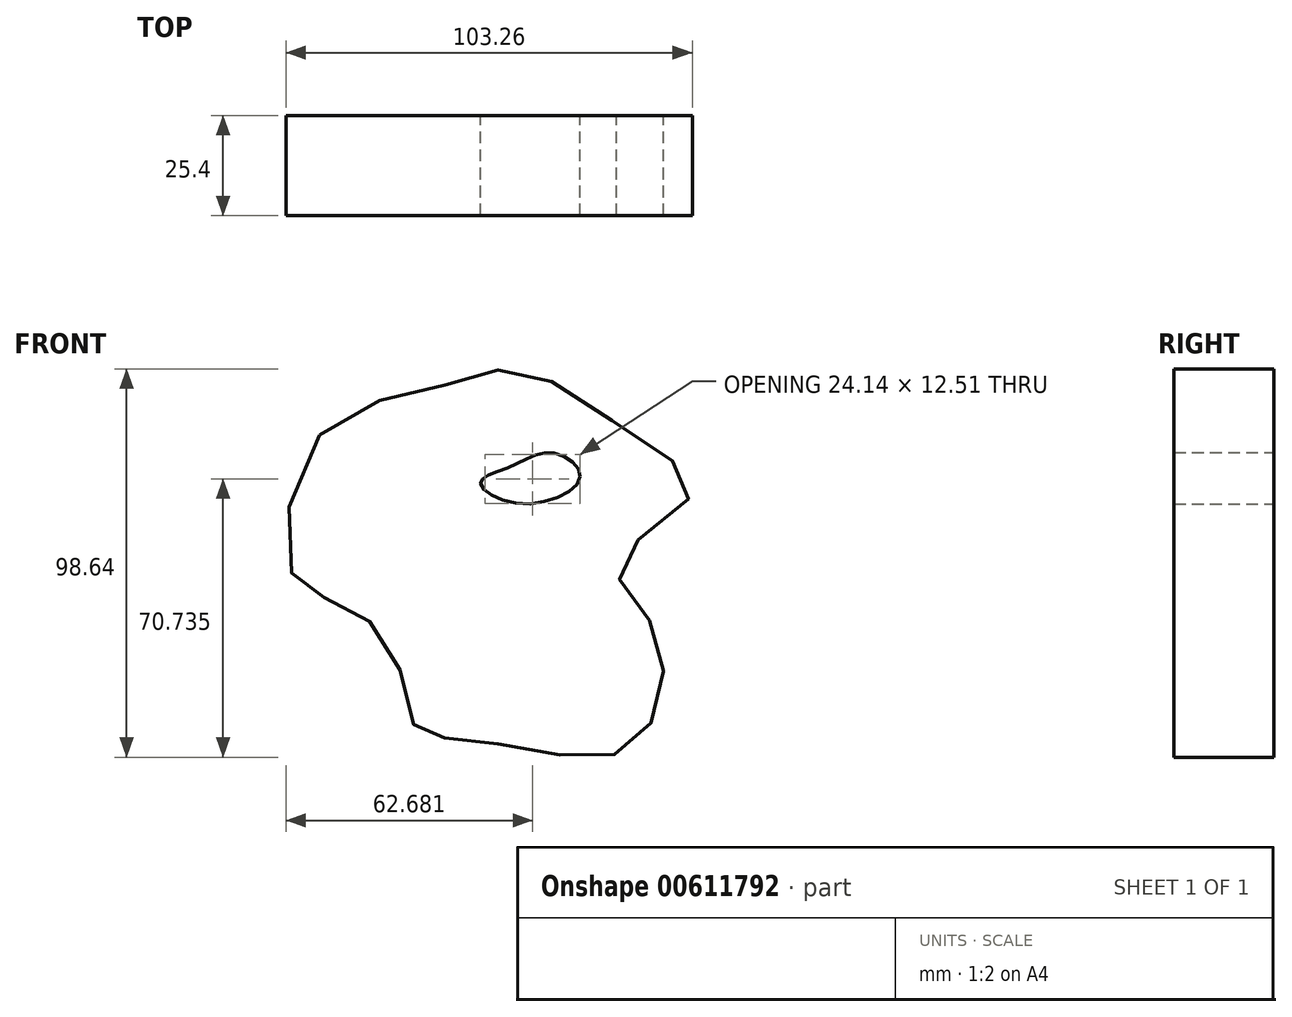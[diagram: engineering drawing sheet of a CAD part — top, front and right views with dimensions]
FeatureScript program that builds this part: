
annotation { "Feature Type Name" : "Feature", "Feature Type Description" : "" }
export const myFeature = defineFeature(function(context is Context, id is Id, definition is map)
    precondition{}
    {
        {
            var Q0;
            Q0=qCreatedBy(makeId("Front.planeOp"),FACE);
            var sketch = newSketch(context, id + "F0", { "sketchPlane" : qUnion([Q0])});
            skFitSpline(sketch, "E0", {"points": [v(-59.1, 47.37) * mm, v(-66.32, 12.48) * mm, v(-56.4, 5.56) * mm, v(-40.76, -6.77) * mm, v(-34.44, -27.52) * mm, v(-25.12, -29.63) * mm, v(0, -33.54) * mm, v(19.7, -32.03) * mm, v(28.12, -15.5) * mm, v(23.01, 2.86) * mm, v(16.7, 15.19) * mm, v(35.34, 32.64) * mm, v(20.6, 47.37) * mm, v(-8.27, 63.92) * mm, v(-28.73, 59.7) * mm, v(-59.1, 47.37) * mm]});
            skSolve(sketch);
        }
        {
            var Q0;
            Q0=makeQuery(id+"F0.imprint","IMPRINT",FACE,{"disambiguationData":[TD([[makeQuery(id+"F0.imprint","IMPRINT",EDGE,{"derivedFrom":sQuery(id+"F0.wireOp",EDGE,"E0")}),1.0]])]});
            extrude(context, id + "F1", {"entities" : qUnion([Q0]), "depth" : 25.4 * mm, "offsetDistance" : 25.4 * mm});
        }
        {
            var Q0;
            Q0=makeQuery(id+"F1.opExtrude","CAP_FACE",FACE,{"disambiguationData":[OSD([sQuery(id+"F0.wireOp",EDGE,"E0")])],"isStart":true});
            var sketch = newSketch(context, id + "F2", { "sketchPlane" : qUnion([Q0])});
            skFitSpline(sketch, "E1", {"points": [v(-7.07, 36.85) * mm, v(0, 42.86) * mm, v(10.98, 39.25) * mm, v(18.2, 35.34) * mm, v(7.67, 29.93) * mm, v(-7.07, 36.85) * mm]});
            skSolve(sketch);
        }
        {
            var Q0;
            Q0=makeQuery(id+"F2.imprint","IMPRINT",FACE,{"disambiguationData":[TD([[makeQuery(id+"F2.imprint","IMPRINT",EDGE,{"derivedFrom":sQuery(id+"F2.wireOp",EDGE,"E1")}),-1.0]])]});
            extrude(context, id + "F3", {"entities" : qUnion([Q0]), "operationType" : NewBodyOperationType.REMOVE, "oppositeDirection" : true, "depth" : 25.4 * mm, "offsetDistance" : 25.4 * mm});
        }
    });
